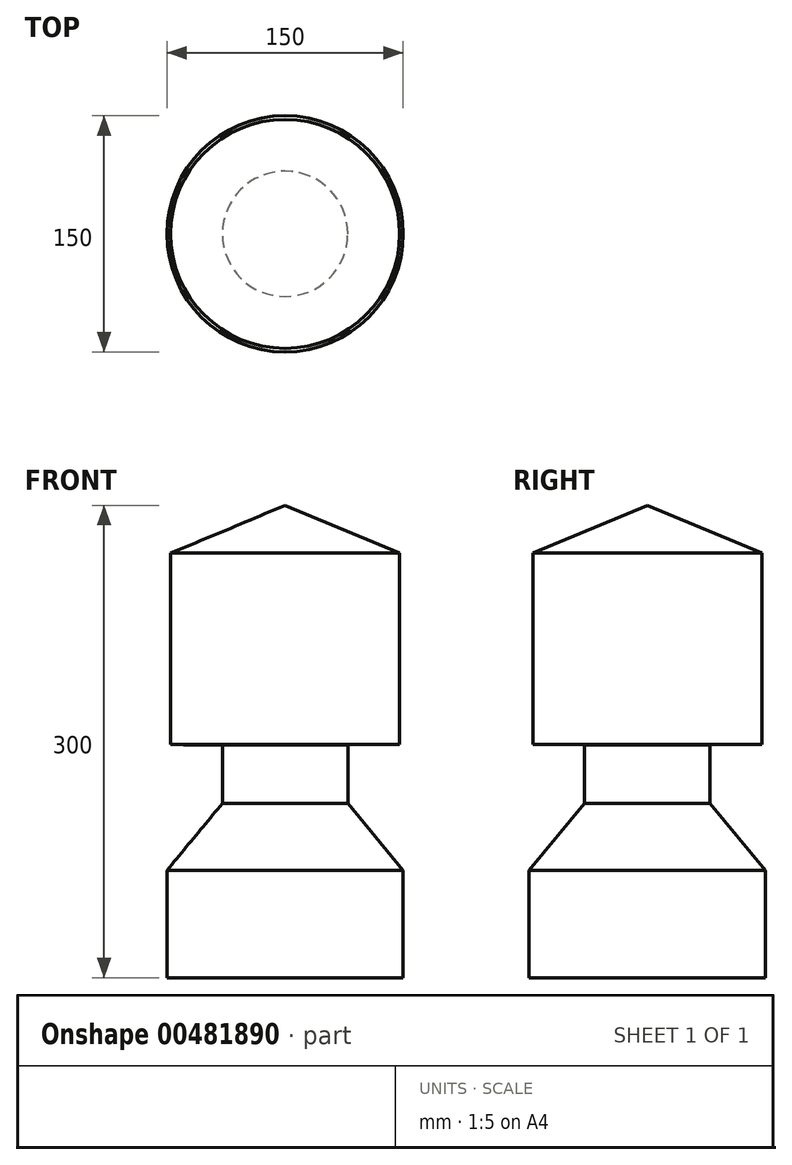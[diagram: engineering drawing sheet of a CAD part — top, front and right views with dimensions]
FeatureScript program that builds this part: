
annotation { "Feature Type Name" : "Feature", "Feature Type Description" : "" }
export const myFeature = defineFeature(function(context is Context, id is Id, definition is map)
    precondition{}
    {
        {
            var Q0;
            Q0=qCreatedBy(makeId("Front.planeOp"),FACE);
            var sketch = newSketch(context, id + "F0", { "sketchPlane" : qUnion([Q0])});
            skLineSegment(sketch, "E0", {"start": v(0, 0) * mm, "end": v(0, 300) * mm});
            skLineSegment(sketch, "E1", {"start": v(0, 0) * mm, "end": v(-75, 0) * mm});
            skLineSegment(sketch, "E2", {"start": v(-75, 0) * mm, "end": v(-75, 68.2) * mm});
            skLineSegment(sketch, "E3", {"start": v(-75, 68.2) * mm, "end": v(-39.83, 110.77) * mm});
            skLineSegment(sketch, "E4", {"start": v(-39.83, 110.77) * mm, "end": v(-39.83, 147.95) * mm});
            skLineSegment(sketch, "E5", {"start": v(-39.83, 147.95) * mm, "end": v(-72.7, 148.06) * mm});
            skLineSegment(sketch, "E6", {"start": v(-72.7, 148.06) * mm, "end": v(-72.7, 269.66) * mm});
            skLineSegment(sketch, "E7", {"start": v(-72.7, 269.66) * mm, "end": v(0, 300) * mm});
            skSolve(sketch);
        }
        {
            var Q0;
            Q0 = qSketchRegion(id + "F0", true);
            var Q1;
            Q1=sQuery(id+"F0.wireOp",EDGE,"E0");
            revolve(context, id + "F1", {"entities" : qUnion([Q0]), "axis" : qUnion([Q1]), "revolveType" : RevolveType.FULL});
        }
    });
